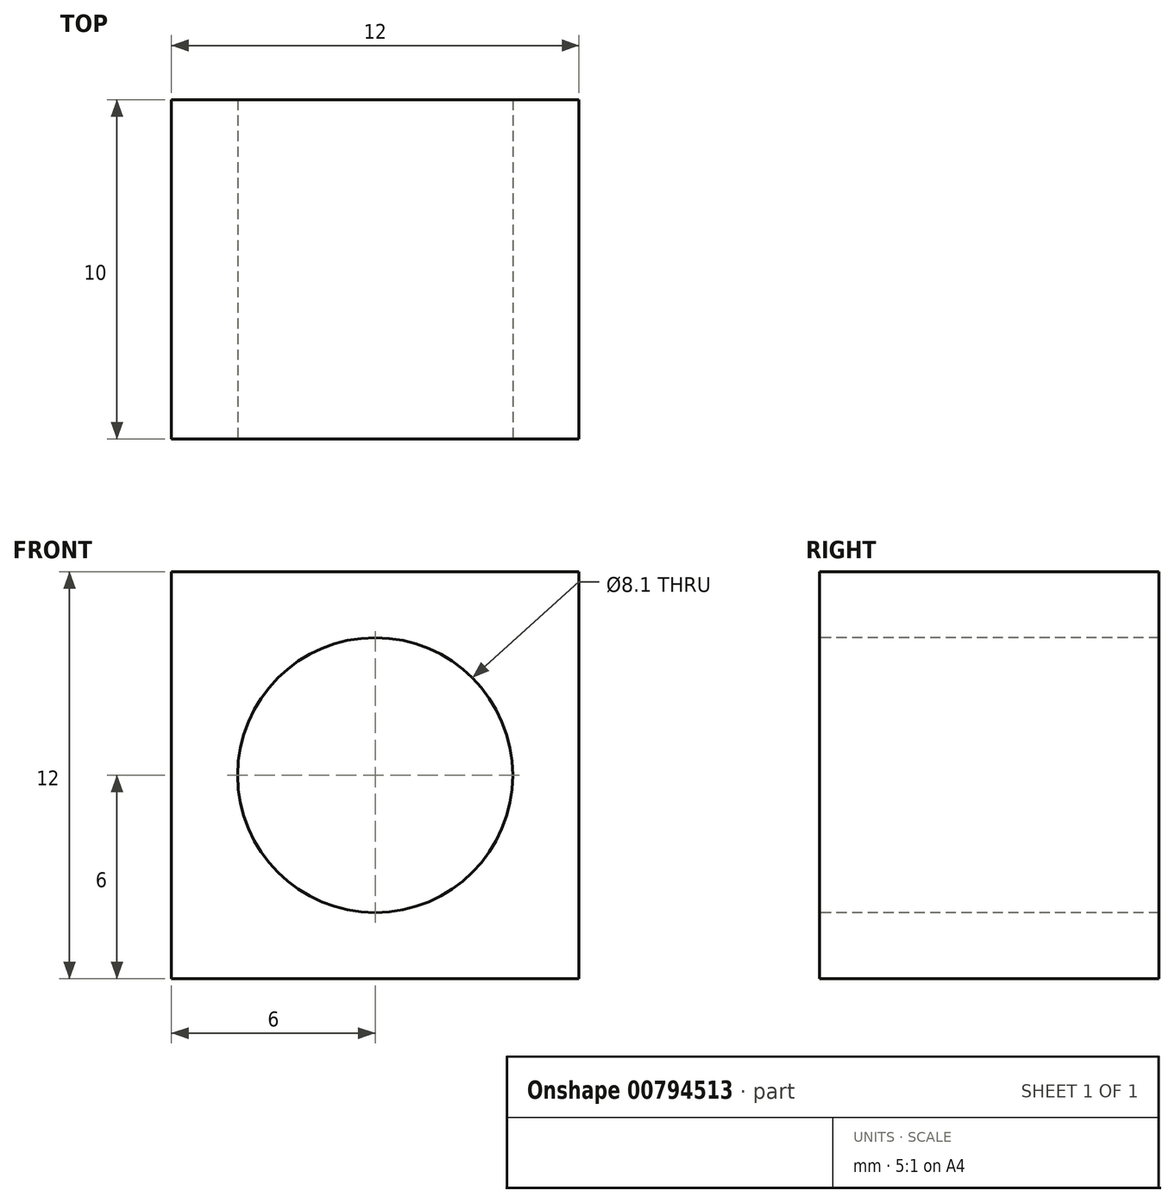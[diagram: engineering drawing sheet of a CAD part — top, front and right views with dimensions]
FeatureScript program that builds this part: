
annotation { "Feature Type Name" : "Feature", "Feature Type Description" : "" }
export const myFeature = defineFeature(function(context is Context, id is Id, definition is map)
    precondition{}
    {
        {
            var Q0;
            Q0=qCreatedBy(makeId("Top.planeOp"),FACE);
            var sketch = newSketch(context, id + "F0", { "sketchPlane" : qUnion([Q0])});
            skLineSegment(sketch, "E0.bottom", {"start": v(6, -5) * mm, "end": v(-6, -5) * mm});
            skLineSegment(sketch, "E0.top", {"start": v(6, 5) * mm, "end": v(-6, 5) * mm});
            skLineSegment(sketch, "E0.left", {"start": v(6, -5) * mm, "end": v(6, 5) * mm});
            skLineSegment(sketch, "E0.right", {"start": v(-6, -5) * mm, "end": v(-6, 5) * mm});
            skPoint(sketch, "E0.middle", {"position": v(0, 0) * mm});
            skSolve(sketch);
        }
        {
            var Q0;
            Q0=makeQuery(id+"F0.imprint","IMPRINT",FACE,{"disambiguationData":[TD([[makeQuery(id+"F0.imprint","IMPRINT",EDGE,{"derivedFrom":sQuery(id+"F0.wireOp",EDGE,"E0.bottom")}),-1.0]])]});
            extrude(context, id + "F1", {"entities" : qUnion([Q0]), "depth" : 12 * mm, "offsetDistance" : 25 * mm});
        }
        {
            var Q0;
            Q0=makeQuery(id+"F1.opExtrude","SWEPT_FACE",FACE,{"disambiguationData":[OSD([sQuery(id+"F0.wireOp",EDGE,"E0.bottom")])]});
            var sketch = newSketch(context, id + "F2", { "sketchPlane" : qUnion([Q0])});
            skLineSegment(sketch, "E1", {"start": v(-6, 12) * mm, "end": v(6, 0) * mm, "construction": true});
            skCircle(sketch, "E2", {"center": v(0, 6) * mm, "radius": 4.05 * mm});
            skSolve(sketch);
        }
        {
            var Q0;
            Q0=makeQuery(id+"F2.imprint","IMPRINT",FACE,{"disambiguationData":[TD([[makeQuery(id+"F2.imprint","IMPRINT",EDGE,{"derivedFrom":sQuery(id+"F2.wireOp",EDGE,"E2")}),1.0]])]});
            extrude(context, id + "F3", {"entities" : qUnion([Q0]), "operationType" : NewBodyOperationType.REMOVE, "oppositeDirection" : true, "depth" : 25 * mm, "offsetDistance" : 25 * mm});
        }
    });
